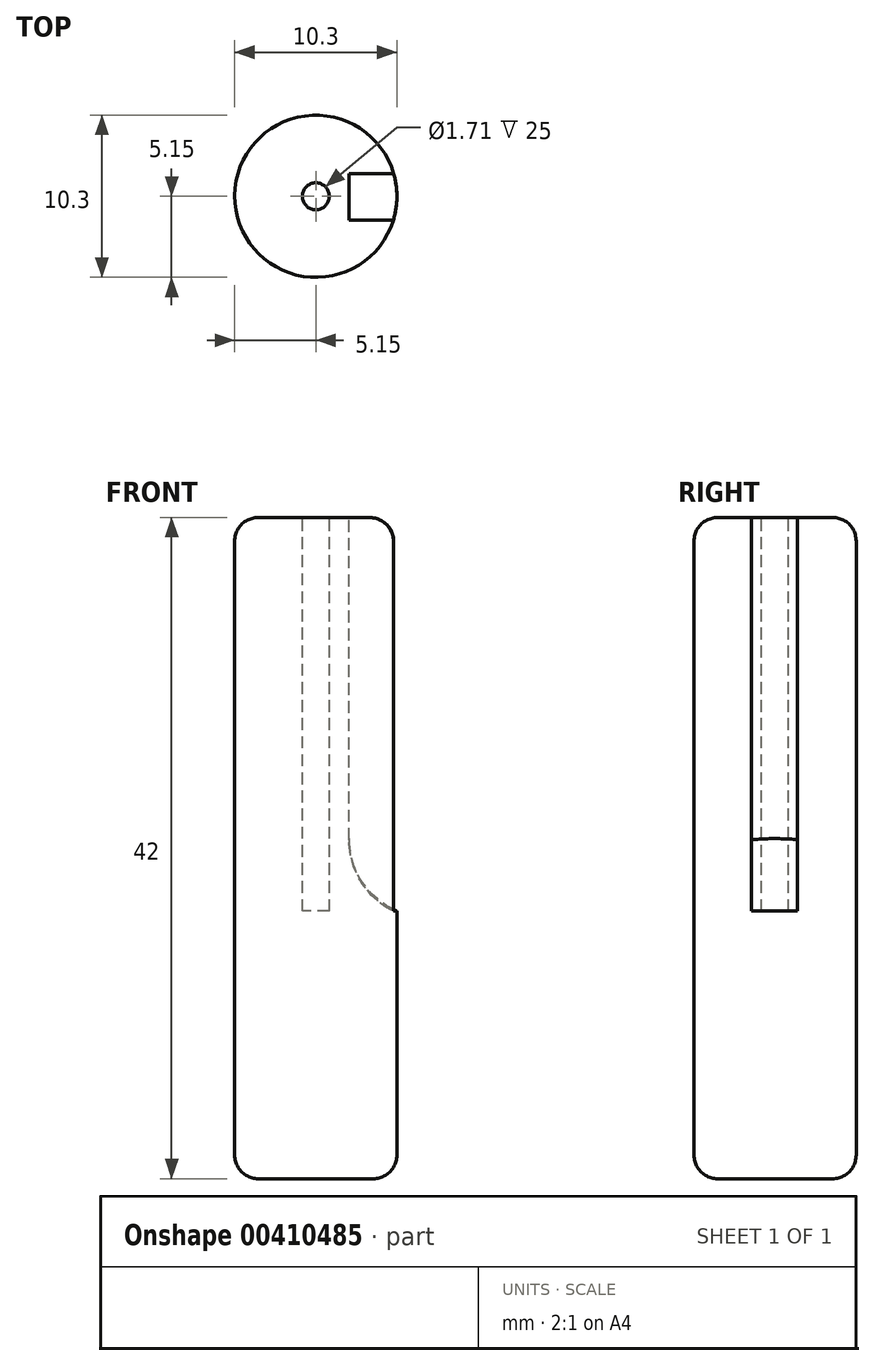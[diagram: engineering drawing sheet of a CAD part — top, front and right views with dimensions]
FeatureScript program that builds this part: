
annotation { "Feature Type Name" : "Feature", "Feature Type Description" : "" }
export const myFeature = defineFeature(function(context is Context, id is Id, definition is map)
    precondition{}
    {
        {
            var Q0;
            Q0=qCreatedBy(makeId("Top.planeOp"),FACE);
            var sketch = newSketch(context, id + "F0", { "sketchPlane" : qUnion([Q0])});
            skCircle(sketch, "E0", {"center": v(0, 0) * mm, "radius": 5.15 * mm});
            skSolve(sketch);
        }
        {
            var Q0;
            Q0 = qSketchRegion(id + "F0", true);
            extrude(context, id + "F1", {"entities" : qUnion([Q0]), "depth" : 42 * mm, "offsetDistance" : 25 * mm});
        }
        {
            var Q0;
            Q0=makeQuery(id+"F1.opExtrude","CAP_FACE",FACE,{"disambiguationData":[OSD([sQuery(id+"F0.wireOp",EDGE,"E0")])],"isStart":false});
            var sketch = newSketch(context, id + "F2", { "sketchPlane" : qUnion([Q0])});
            skCircle(sketch, "E1", {"center": v(0, 0) * mm, "radius": 0.86 * mm});
            skLineSegment(sketch, "E2.bottom", {"start": v(2.12, 1.42) * mm, "end": v(5.91, 1.42) * mm});
            skLineSegment(sketch, "E2.top", {"start": v(2.12, -1.5) * mm, "end": v(5.91, -1.5) * mm});
            skLineSegment(sketch, "E2.left", {"start": v(2.12, 1.42) * mm, "end": v(2.12, -1.5) * mm});
            skLineSegment(sketch, "E2.right", {"start": v(5.91, 1.42) * mm, "end": v(5.91, -1.5) * mm});
            skSolve(sketch);
        }
        {
            var Q0;
            Q0 = qSketchRegion(id + "F2", true);
            extrude(context, id + "F3", {"entities" : qUnion([Q0]), "operationType" : NewBodyOperationType.REMOVE, "oppositeDirection" : true, "depth" : 25 * mm, "offsetDistance" : 25 * mm});
        }
        {
            var Q0;
            Q0=makeQuery(id+"F3.boolean.opBoolean","COPY",EDGE,{"derivedFrom":makeQuery(id+"F3.opExtrude","CAP_EDGE",EDGE,{"disambiguationData":[OSD([sQuery(id+"F2.wireOp",EDGE,"E2.left")])],"isStart":false})});
            fillet(context, id + "F4", {"entities" : qUnion([Q0]), "radius" : 5 * mm, "tangentPropagation" : true, "allowEdgeOverflow" : false});
        }
        {
            var Q0;
            Q0=makeQuery(id+"F1.opExtrude","CAP_EDGE",EDGE,{"disambiguationData":[OSD([sQuery(id+"F0.wireOp",EDGE,"E0")])],"isStart":false});
            var Q1;
            Q1=makeQuery(id+"F1.opExtrude","CAP_EDGE",EDGE,{"disambiguationData":[OSD([sQuery(id+"F0.wireOp",EDGE,"E0")])],"isStart":true});
            fillet(context, id + "F5", {"entities" : qUnion([Q0, Q1]), "radius" : 1.5 * mm, "tangentPropagation" : true, "allowEdgeOverflow" : false});
        }
    });
